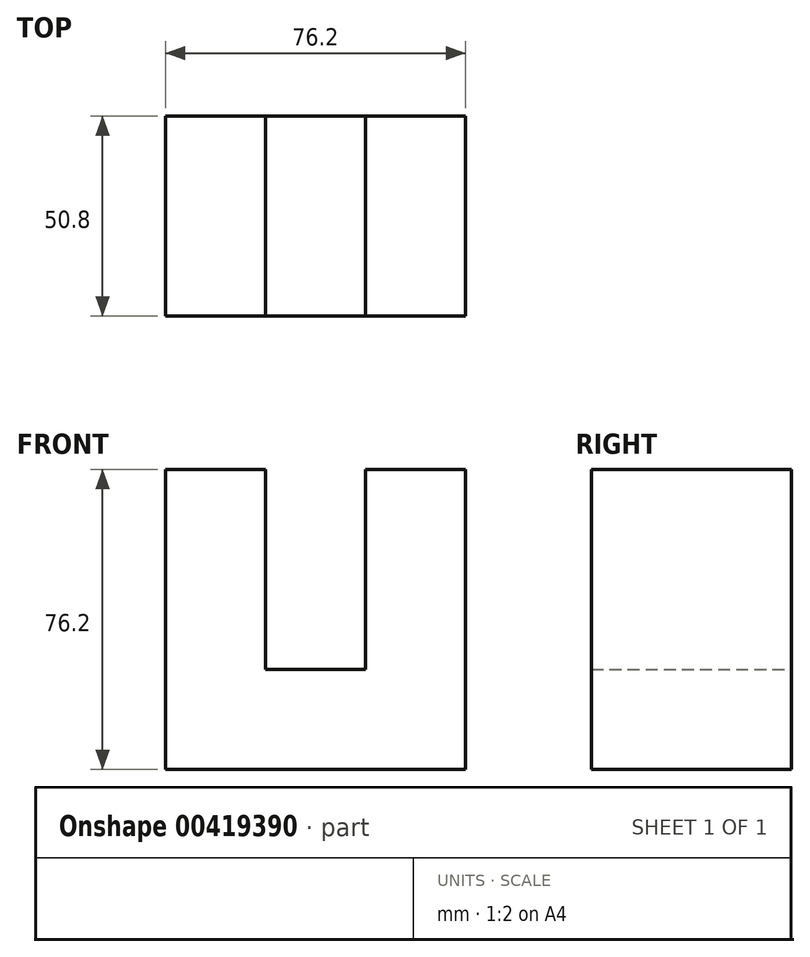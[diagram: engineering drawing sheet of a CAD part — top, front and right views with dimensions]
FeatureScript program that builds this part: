
annotation { "Feature Type Name" : "Feature", "Feature Type Description" : "" }
export const myFeature = defineFeature(function(context is Context, id is Id, definition is map)
    precondition{}
    {
        {
            var Q0;
            Q0=qCreatedBy(makeId("Front.planeOp"),FACE);
            var sketch = newSketch(context, id + "F0", { "sketchPlane" : qUnion([Q0])});
            skLineSegment(sketch, "E0", {"start": v(-63.67, 50.8) * mm, "end": v(-63.67, -25.4) * mm});
            skLineSegment(sketch, "E1", {"start": v(-63.67, -25.4) * mm, "end": v(12.53, -25.4) * mm});
            skLineSegment(sketch, "E2", {"start": v(12.53, -25.4) * mm, "end": v(12.53, 50.8) * mm});
            skLineSegment(sketch, "E3", {"start": v(12.53, 50.8) * mm, "end": v(-12.87, 50.8) * mm});
            skLineSegment(sketch, "E4", {"start": v(-12.87, 50.8) * mm, "end": v(-12.87, 0) * mm});
            skLineSegment(sketch, "E5", {"start": v(-12.87, 0) * mm, "end": v(-38.27, 0) * mm});
            skLineSegment(sketch, "E6", {"start": v(-38.27, 0) * mm, "end": v(-38.27, 50.8) * mm});
            skLineSegment(sketch, "E7", {"start": v(-38.27, 50.8) * mm, "end": v(-63.67, 50.8) * mm});
            skSolve(sketch);
        }
        {
            var Q0;
            Q0 = qSketchRegion(id + "F0", true);
            extrude(context, id + "F1", {"entities" : qUnion([Q0]), "depth" : 50.8 * mm});
        }
    });
